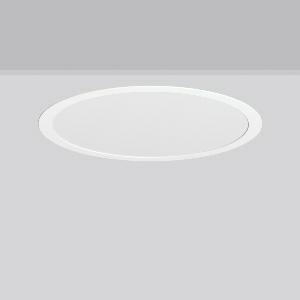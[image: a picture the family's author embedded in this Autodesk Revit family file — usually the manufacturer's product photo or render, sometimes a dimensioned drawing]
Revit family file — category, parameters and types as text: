
# Revit family: toledo_flat__round_e_901812_002_76_5744
name_source: partatom
category: Lighting Fixtures
units: mm (PartAtom-declared; Revit-internal decimal feet)

## family parameters
Cut with Voids When Loaded = No
Host = Face
Light Source = No
Part Type = Normal
Room Calculation Point = No
Round Connector Dimension = Use Diameter
Shared = No

## types (1)
- MultiLumen 1 (1 x LED Modul 840, 3050 lm, 4000)
    Apparent Load = 22 VA
    CIE Flux Codes = 47 79 96 100 100
    Color Rendering = 80
    Color Temperature = 4000
    Default Elevation = 1800 mm
    Description = Series: TOLEDO FLAT+ round
Flexible round recessed multifunction downlight. Housing: sheet steel, powder-coated. Luminaire frame: aluminium, powder-coated. Light guide and diffuser made of non-yellowing PMMA, opal matt. LED backlight technology for homogeneous illumination of the entire light-emitting surface. MultiColour: Colour temperature individually adjustable either 3000 K or 4000 K via switching element. Factory setting is 4000 K. MultiLumen: 4 steps adjustable luminous flux. Factory setting is step 2. Suitable for Recessed ceiling mounting. Ceiling installation with spring system. Can be directly covered with thermal insulation material (applies only to the lower lumen levels). Including separate LED converter with connecting cable 250 mm. Suitable for through wiring as standard. Surface mounted housing as accessory for all sizes. 
Colour: white
Diameter: 470 mm
Height: 2 mm
Cut-out diameter: 457 mm
Recess height: 70 mm
Luminaire: recess height: 41 mm
Lamp: LED
Socket: without socket
Colour temperature: 3000K, 4000K
Colour rendering index (CRI): 80
System power: 22 W
Rated luminous flux: 3050 lm
Luminous efficiency: 139 lm/W
System power 2: 26 W
Rated luminous flux 2: 3550 lm
Luminous efficiency 2: 137 lm/W
System power 3: 30 W
Rated luminous flux 3: 4000 lm
Luminous efficiency 3: 133 lm/W
System power 4: 33 W
Rated luminous flux 4: 4450 lm
Luminous efficiency 4: 135 lm/W
Control gear: Converter, dimmable, DALI
Protection class: II
Type of protection: IP 54
    Height = 0 mm  [stored 0 ft]
    Lamp = 1 x LED Modul 840
    Lamp Light Flux = 3050 lm
    Lamp count = 1
    Length = 470 mm
    Lifetime = 50000 h
    Luminous efficacy = 139 lm/W
    Manufacturer = RZB
    ModVariant = No
    Model = 901812.002.76
    Mounting Place = Ceiling
    Mounting Type = Recessed
    Number of Poles = 1
    OnlyDefault = Yes
    Power Factor = 1
    Product Name = TOLEDO FLAT+ round E
    Product group = Recessed downlights
    ProductGroupID = 402
    Protection Class = Protection class II
    Protection Degree = Degree of protection
    RLX_Detail_Level = 1
    RLX_Emergency_Light_Flux = 0 lm
    RLX_Emergency_Type = 0
    RLX_Emergency_Type_DB = No
    RlxData = <blob elided: 35477 chars, md5=13c36540>
    Socket = socket
    Standby Power = 0 W
    System Light Flux = 3050 lm
    System Power = 22 W
    Type Comments = MultiLumen 1
    Type Image = 901812.002.jpg
    URL = http://relux.com
    VarID = multilumen_1
    Voltage = 0 V
    Weight = 0.00 kg
    Width = 0 mm  [stored 0 ft]

note: [stored X ft] marks values corroborated as IEEE doubles in the binary element streams (Revit-internal decimal feet)

## geometry (parser evidence)
native form markers: Blend x4, Sweep x8
no freeform markers — native parametric forms only
